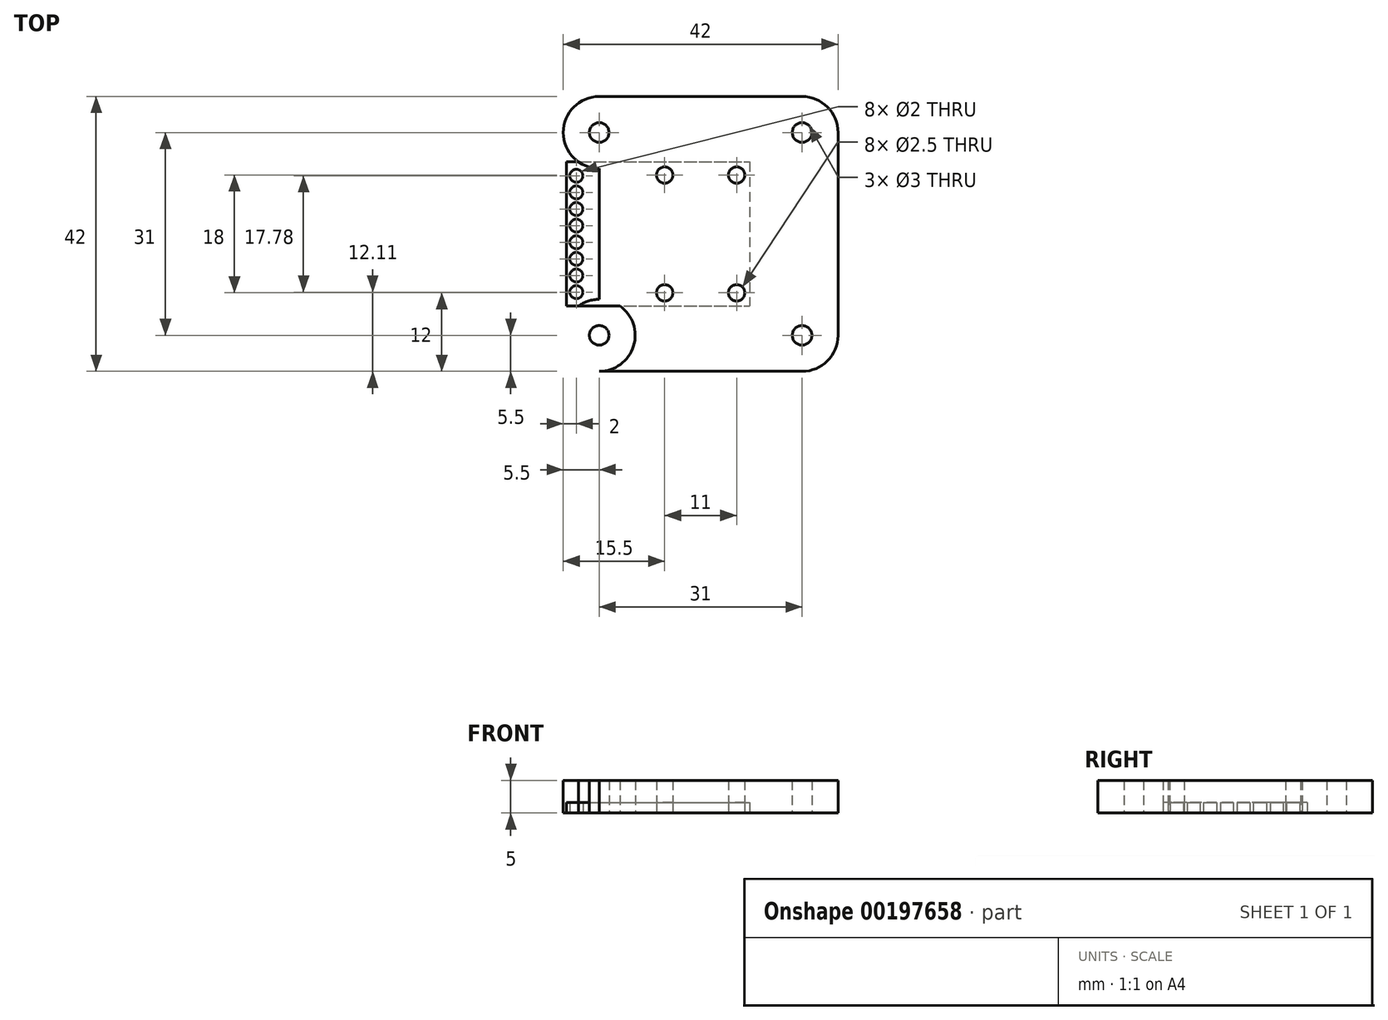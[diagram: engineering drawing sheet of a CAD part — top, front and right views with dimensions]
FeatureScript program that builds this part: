
annotation { "Feature Type Name" : "Feature", "Feature Type Description" : "" }
export const myFeature = defineFeature(function(context is Context, id is Id, definition is map)
    precondition{}
    {
        {
            var Q0;
            Q0=qCreatedBy(makeId("Top.planeOp"),FACE);
            var sketch = newSketch(context, id + "F0", { "sketchPlane" : qUnion([Q0])});
            skLineSegment(sketch, "E0.bottom", {"start": v(15.5, -21) * mm, "end": v(-15.5, -21) * mm});
            skLineSegment(sketch, "E0.top", {"start": v(15.5, 21) * mm, "end": v(-15.5, 21) * mm});
            skLineSegment(sketch, "E0.left", {"start": v(21, -15.5) * mm, "end": v(21, 15.5) * mm});
            skLineSegment(sketch, "E0.right", {"start": v(-21, -15.5) * mm, "end": v(-21, 15.5) * mm});
            skPoint(sketch, "E0.middle", {"position": v(0, 0) * mm});
            skCircle(sketch, "E1", {"center": v(-15.5, 15.5) * mm, "radius": 1.5 * mm});
            skCircle(sketch, "E2.MirrorC", {"center": v(15.5, 15.5) * mm, "radius": 1.5 * mm});
            skCircle(sketch, "E3.MirrorC", {"center": v(-15.5, -15.5) * mm, "radius": 1.5 * mm});
            skCircle(sketch, "E4.MirrorC", {"center": v(15.5, -15.5) * mm, "radius": 1.5 * mm});
            skPoint(sketch, "E5.visualSharp", {"position": v(-21, 21) * mm});
            skArc(sketch, "E5.filletArc", {"start": v(-15.5, 21) * mm, "mid": v(-19.39, 19.39) * mm, "end": v(-21, 15.5) * mm});
            skPoint(sketch, "E6.visualSharp", {"position": v(21, 21) * mm});
            skArc(sketch, "E6.filletArc", {"start": v(21, 15.5) * mm, "mid": v(19.39, 19.39) * mm, "end": v(15.5, 21) * mm});
            skPoint(sketch, "E7.visualSharp", {"position": v(-21, -21) * mm});
            skArc(sketch, "E7.filletArc", {"start": v(-21, -15.5) * mm, "mid": v(-19.39, -19.39) * mm, "end": v(-15.5, -21) * mm});
            skPoint(sketch, "E8.visualSharp", {"position": v(21, -21) * mm});
            skArc(sketch, "E8.filletArc", {"start": v(15.5, -21) * mm, "mid": v(19.39, -19.39) * mm, "end": v(21, -15.5) * mm});
            skLineSegment(sketch, "E9.bottom", {"start": v(-20.5, 11) * mm, "end": v(7.5, 11) * mm});
            skLineSegment(sketch, "E9.top", {"start": v(-20.5, -11) * mm, "end": v(7.5, -11) * mm});
            skLineSegment(sketch, "E9.left", {"start": v(-20.5, 11) * mm, "end": v(-20.5, -11) * mm});
            skLineSegment(sketch, "E9.right", {"start": v(7.5, 11) * mm, "end": v(7.5, -11) * mm});
            skPoint(sketch, "E10", {"position": v(-20.5, 0) * mm});
            skLineSegment(sketch, "E11.bottom", {"start": v(-5.5, 9) * mm, "end": v(5.5, 9) * mm});
            skLineSegment(sketch, "E11.top", {"start": v(-5.5, -9) * mm, "end": v(5.5, -9) * mm});
            skLineSegment(sketch, "E11.left", {"start": v(-5.5, 9) * mm, "end": v(-5.5, -9) * mm});
            skLineSegment(sketch, "E11.right", {"start": v(5.5, 9) * mm, "end": v(5.5, -9) * mm});
            skCircle(sketch, "E12", {"center": v(-5.5, 9) * mm, "radius": 1.25 * mm});
            skCircle(sketch, "E13", {"center": v(5.5, 9) * mm, "radius": 1.25 * mm});
            skCircle(sketch, "E14", {"center": v(-5.5, -9) * mm, "radius": 1.25 * mm});
            skCircle(sketch, "E15", {"center": v(5.5, -9) * mm, "radius": 1.25 * mm});
            skPoint(sketch, "E16", {"position": v(-5.5, 0) * mm});
            skLineSegment(sketch, "E17", {"start": v(-19, 11) * mm, "end": v(-19, -11) * mm});
            skCircle(sketch, "E18", {"center": v(-19, 8.89) * mm, "radius": 1 * mm});
            skCircle(sketch, "E19.0.1.0", {"center": v(-19, 6.35) * mm, "radius": 1 * mm});
            skCircle(sketch, "E19.0.2.0", {"center": v(-19, 3.8) * mm, "radius": 1 * mm});
            skCircle(sketch, "E19.0.3.0", {"center": v(-19, 1.27) * mm, "radius": 1 * mm});
            skCircle(sketch, "E19.0.4.0", {"center": v(-19, -1.27) * mm, "radius": 1 * mm});
            skCircle(sketch, "E19.0.5.0", {"center": v(-19, -3.81) * mm, "radius": 1 * mm});
            skCircle(sketch, "E19.0.6.0", {"center": v(-19, -6.35) * mm, "radius": 1 * mm});
            skCircle(sketch, "E19.0.7.0", {"center": v(-19, -8.9) * mm, "radius": 1 * mm});
            skLineSegment(sketch, "E19.direction1", {"start": v(-19, 8.89) * mm, "end": v(6, 8.89) * mm, "construction": true});
            skLineSegment(sketch, "E19.direction2", {"start": v(-19, 8.89) * mm, "end": v(-19, 6.35) * mm, "construction": true});
            skPoint(sketch, "E20", {"position": v(0, -9) * mm});
            skCircle(sketch, "E21", {"center": v(-15.5, 15.5) * mm, "radius": 5.5 * mm});
            skCircle(sketch, "E22", {"center": v(-15.5, -15.5) * mm, "radius": 5.5 * mm});
            skLineSegment(sketch, "E23", {"start": v(-15.5, 15.5) * mm, "end": v(-15.5, -15.5) * mm});
            skSolve(sketch);
        }
        {
            var Q0;
            Q0=makeQuery(id+"F0.imprint","IMPRINT",FACE,{"disambiguationData":[TD([[makeQuery(id+"F0.imprint","IMPRINT",EDGE,{"derivedFrom":sQuery(id+"F0.wireOp",EDGE,"E1")}),-1.0]])]});
            var Q1;
            Q1=makeQuery(id+"F0.imprint","IMPRINT",FACE,{"disambiguationData":[TD([[makeQuery(id+"F0.imprint","IMPRINT",EDGE,{"derivedFrom":sQuery(id+"F0.wireOp",EDGE,"E3.MirrorC")}),1.0]])]});
            var Q2;
            {var subQ7=sQuery(id+"F0.wireOp",EDGE,"E0.bottom");Q2=makeQuery(id+"F0.imprint","IMPRINT",FACE,{"disambiguationData":[TD([[makeQuery(id+"F0.imprint","IMPRINT",EDGE,{"derivedFrom":subQ7}),-1.0]])]});}
            var Q3;
            {var subQ21=sQuery(id+"F0.wireOp",EDGE,"E9.right");Q3=makeQuery(id+"F0.imprint","IMPRINT",FACE,{"disambiguationData":[TD([[makeQuery(id+"F0.imprint","IMPRINT",EDGE,{"derivedFrom":subQ21}),-1.0]])]});}
            var Q4;
            {var subQ0=sQuery(id+"F0.wireOp",EDGE,"E23");var subQ1=sQuery(id+"F0.wireOp",EDGE,"E9.bottom");var subQ2=makeQuery(id+"F0.imprint","INTERSECT",VERTEX,{"derivedFrom":[subQ1,subQ0]});Q4=makeQuery(id+"F0.imprint","IMPRINT",FACE,{"disambiguationData":[TD([[makeQuery(id+"F0.imprint","IMPRINT",EDGE,{"disambiguationData":[TD([[subQ2,-1.0]])],"derivedFrom":subQ1}),-1.0]])]});}
            var Q5;
            {var subQ0=sQuery(id+"F0.wireOp",EDGE,"E23");var subQ1=sQuery(id+"F0.wireOp",EDGE,"E9.top");var subQ2=makeQuery(id+"F0.imprint","INTERSECT",VERTEX,{"derivedFrom":[subQ1,subQ0]});Q5=makeQuery(id+"F0.imprint","IMPRINT",FACE,{"disambiguationData":[TD([[makeQuery(id+"F0.imprint","IMPRINT",EDGE,{"disambiguationData":[TD([[subQ2,-1.0]])],"derivedFrom":subQ1}),1.0]])]});}
            var Q6;
            {var subQ0=sQuery(id+"F0.wireOp",EDGE,"E23");var subQ1=sQuery(id+"F0.wireOp",EDGE,"E9.bottom");var subQ2=makeQuery(id+"F0.imprint","INTERSECT",VERTEX,{"derivedFrom":[subQ1,subQ0]});Q6=makeQuery(id+"F0.imprint","IMPRINT",FACE,{"disambiguationData":[TD([[makeQuery(id+"F0.imprint","IMPRINT",EDGE,{"disambiguationData":[TD([[subQ2,1.0]])],"derivedFrom":subQ1}),-1.0]])]});}
            var Q7;
            {var subQ0=sQuery(id+"F0.wireOp",EDGE,"E23");var subQ1=sQuery(id+"F0.wireOp",EDGE,"E9.top");var subQ2=makeQuery(id+"F0.imprint","INTERSECT",VERTEX,{"derivedFrom":[subQ1,subQ0]});Q7=makeQuery(id+"F0.imprint","IMPRINT",FACE,{"disambiguationData":[TD([[makeQuery(id+"F0.imprint","IMPRINT",EDGE,{"disambiguationData":[TD([[subQ2,1.0]])],"derivedFrom":subQ1}),1.0]])]});}
            var Q8;
            {var subQ0=sQuery(id+"F0.wireOp",EDGE,"E12");var subQ5=sQuery(id+"F0.wireOp",EDGE,"E11.bottom");var subQ6=makeQuery(id+"F0.imprint","INTERSECT",VERTEX,{"derivedFrom":[subQ5,subQ0]});Q8=makeQuery(id+"F0.imprint","IMPRINT",FACE,{"disambiguationData":[TD([[makeQuery(id+"F0.imprint","IMPRINT",EDGE,{"disambiguationData":[TD([[subQ6,-1.0]])],"derivedFrom":subQ5}),-1.0]])]});}
            extrude(context, id + "F1", {"entities" : qUnion([Q0, Q1, Q2, Q3, Q4, Q5, Q6, Q7, Q8]), "depth" : 5 * mm});
        }
        {
            var Q0;
            {var subQ21=sQuery(id+"F0.wireOp",EDGE,"E9.right");Q0=makeQuery(id+"F0.imprint","IMPRINT",FACE,{"disambiguationData":[TD([[makeQuery(id+"F0.imprint","IMPRINT",EDGE,{"derivedFrom":subQ21}),-1.0]])]});}
            var Q1;
            {var subQ0=sQuery(id+"F0.wireOp",EDGE,"E12");var subQ5=sQuery(id+"F0.wireOp",EDGE,"E11.bottom");var subQ6=makeQuery(id+"F0.imprint","INTERSECT",VERTEX,{"derivedFrom":[subQ5,subQ0]});Q1=makeQuery(id+"F0.imprint","IMPRINT",FACE,{"disambiguationData":[TD([[makeQuery(id+"F0.imprint","IMPRINT",EDGE,{"disambiguationData":[TD([[subQ6,-1.0]])],"derivedFrom":subQ5}),-1.0]])]});}
            var Q2;
            {var subQ1=sQuery(id+"F0.wireOp",EDGE,"E17");var subQ25=sQuery(id+"F0.wireOp",EDGE,"E9.bottom");var subQ26=makeQuery(id+"F0.imprint","INTERSECT",VERTEX,{"derivedFrom":[subQ25,subQ1]});Q2=makeQuery(id+"F0.imprint","IMPRINT",FACE,{"disambiguationData":[TD([[makeQuery(id+"F0.imprint","IMPRINT",EDGE,{"disambiguationData":[TD([[subQ26,-1.0]])],"derivedFrom":subQ25}),-1.0]])]});}
            var Q3;
            {var subQ5=sQuery(id+"F0.wireOp",EDGE,"E9.left");Q3=makeQuery(id+"F0.imprint","IMPRINT",FACE,{"disambiguationData":[TD([[makeQuery(id+"F0.imprint","IMPRINT",EDGE,{"derivedFrom":subQ5}),1.0]])]});}
            var Q4;
            {var subQ0=sQuery(id+"F0.wireOp",EDGE,"E23");var subQ1=sQuery(id+"F0.wireOp",EDGE,"E9.top");var subQ2=makeQuery(id+"F0.imprint","INTERSECT",VERTEX,{"derivedFrom":[subQ1,subQ0]});Q4=makeQuery(id+"F0.imprint","IMPRINT",FACE,{"disambiguationData":[TD([[makeQuery(id+"F0.imprint","IMPRINT",EDGE,{"disambiguationData":[TD([[subQ2,1.0]])],"derivedFrom":subQ1}),1.0]])]});}
            var Q5;
            {var subQ0=sQuery(id+"F0.wireOp",EDGE,"E23");var subQ1=sQuery(id+"F0.wireOp",EDGE,"E9.top");var subQ2=makeQuery(id+"F0.imprint","INTERSECT",VERTEX,{"derivedFrom":[subQ1,subQ0]});Q5=makeQuery(id+"F0.imprint","IMPRINT",FACE,{"disambiguationData":[TD([[makeQuery(id+"F0.imprint","IMPRINT",EDGE,{"disambiguationData":[TD([[subQ2,-1.0]])],"derivedFrom":subQ1}),1.0]])]});}
            var Q6;
            {var subQ0=sQuery(id+"F0.wireOp",EDGE,"E23");var subQ1=sQuery(id+"F0.wireOp",EDGE,"E9.bottom");var subQ2=makeQuery(id+"F0.imprint","INTERSECT",VERTEX,{"derivedFrom":[subQ1,subQ0]});Q6=makeQuery(id+"F0.imprint","IMPRINT",FACE,{"disambiguationData":[TD([[makeQuery(id+"F0.imprint","IMPRINT",EDGE,{"disambiguationData":[TD([[subQ2,1.0]])],"derivedFrom":subQ1}),-1.0]])]});}
            var Q7;
            {var subQ0=sQuery(id+"F0.wireOp",EDGE,"E23");var subQ1=sQuery(id+"F0.wireOp",EDGE,"E9.bottom");var subQ2=makeQuery(id+"F0.imprint","INTERSECT",VERTEX,{"derivedFrom":[subQ1,subQ0]});Q7=makeQuery(id+"F0.imprint","IMPRINT",FACE,{"disambiguationData":[TD([[makeQuery(id+"F0.imprint","IMPRINT",EDGE,{"disambiguationData":[TD([[subQ2,-1.0]])],"derivedFrom":subQ1}),-1.0]])]});}
            extrude(context, id + "F2", {"entities" : qUnion([Q0, Q1, Q2, Q3, Q4, Q5, Q6, Q7]), "depth" : 1.6 * mm});
        }
    });
